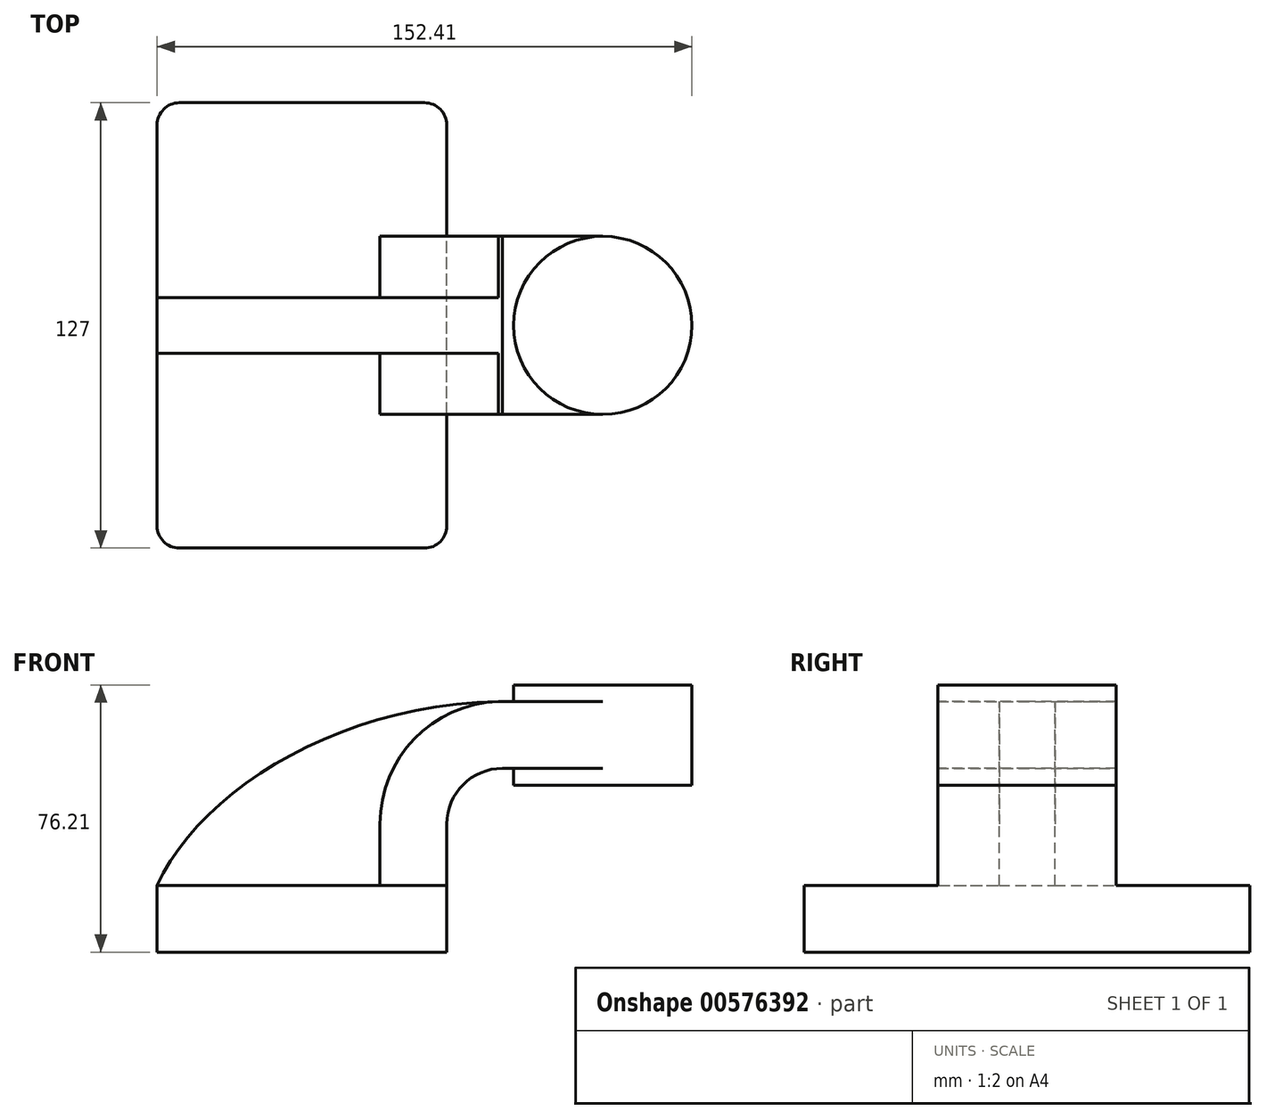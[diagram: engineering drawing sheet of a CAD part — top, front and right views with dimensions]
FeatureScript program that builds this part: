
annotation { "Feature Type Name" : "Feature", "Feature Type Description" : "" }
export const myFeature = defineFeature(function(context is Context, id is Id, definition is map)
    precondition{}
    {
        {
            var Q0;
            Q0=qCreatedBy(makeId("Front.planeOp"),FACE);
            var sketch = newSketch(context, id + "F0", { "sketchPlane" : qUnion([Q0])});
            skLineSegment(sketch, "E0.bottom", {"start": v(41.28, 9.52) * mm, "end": v(-41.28, 9.53) * mm});
            skLineSegment(sketch, "E0.top", {"start": v(41.28, -9.53) * mm, "end": v(-41.27, -9.52) * mm});
            skLineSegment(sketch, "E0.left", {"start": v(41.28, 9.52) * mm, "end": v(41.28, -9.53) * mm});
            skLineSegment(sketch, "E0.right", {"start": v(-41.28, 9.52) * mm, "end": v(-41.28, -9.52) * mm});
            skPoint(sketch, "E0.middle", {"position": v(0, 0) * mm});
            skLineSegment(sketch, "E1.bottom", {"start": v(111.13, 66.67) * mm, "end": v(60.33, 66.67) * mm});
            skLineSegment(sketch, "E1.top", {"start": v(111.13, 38.1) * mm, "end": v(60.33, 38.1) * mm});
            skLineSegment(sketch, "E1.left", {"start": v(111.13, 66.67) * mm, "end": v(111.13, 38.1) * mm});
            skLineSegment(sketch, "E1.right", {"start": v(60.33, 66.67) * mm, "end": v(60.33, 38.1) * mm});
            skPoint(sketch, "E1.middle", {"position": v(85.73, 52.39) * mm});
            skLineSegment(sketch, "E2", {"start": v(41.28, 9.52) * mm, "end": v(41.28, 27) * mm});
            skArc(sketch, "E3", {"start": v(41.28, 27) * mm, "mid": v(45.92, 38.23) * mm, "end": v(57.15, 42.88) * mm});
            skLineSegment(sketch, "E4", {"start": v(57.15, 42.88) * mm, "end": v(85.73, 42.88) * mm});
            skLineSegment(sketch, "E5.0", {"start": v(57.15, 61.93) * mm, "end": v(85.73, 61.93) * mm});
            skArc(sketch, "E5.1", {"start": v(22.23, 27) * mm, "mid": v(32.45, 51.7) * mm, "end": v(57.15, 61.93) * mm});
            skLineSegment(sketch, "E5.2", {"start": v(22.22, 9.52) * mm, "end": v(22.22, 27) * mm});
            skLineSegment(sketch, "E6", {"start": v(85.73, 38.1) * mm, "end": v(85.73, 66.67) * mm});
            skFitSpline(sketch, "E7", {"points": [v(-41.28, 9.52) * mm, v(57.15, 61.93) * mm], "startDerivative": vector(37.56, 80.88) * mm, "endDerivative": vector(141.46, 1.83) * mm});
            skSolve(sketch);
        }
        {
            var Q0;
            Q0=makeQuery(id+"F0.imprint","IMPRINT",FACE,{"disambiguationData":[TD([[makeQuery(id+"F0.imprint","IMPRINT",EDGE,{"derivedFrom":sQuery(id+"F0.wireOp",EDGE,"E0.top")}),-1.0]])]});
            extrude(context, id + "F1", {"entities" : qUnion([Q0]), "endBound" : BoundingType.SYMMETRIC, "depth" : 127 * mm, "offsetDistance" : 25.4 * mm});
        }
        {
            var Q0;
            {var subQ1=sQuery(id+"F0.wireOp",EDGE,"E2");Q0=makeQuery(id+"F0.imprint","IMPRINT",FACE,{"disambiguationData":[TD([[makeQuery(id+"F0.imprint","IMPRINT",EDGE,{"derivedFrom":subQ1}),1.0]])]});}
            var Q1;
            {var subQ0=sQuery(id+"F0.wireOp",EDGE,"E5.0");var subQ1=sQuery(id+"F0.wireOp",EDGE,"E1.right");var subQ2=makeQuery(id+"F0.imprint","INTERSECT",VERTEX,{"derivedFrom":[subQ1,subQ0]});Q1=makeQuery(id+"F0.imprint","IMPRINT",FACE,{"disambiguationData":[TD([[makeQuery(id+"F0.imprint","IMPRINT",EDGE,{"disambiguationData":[TD([[subQ2,-1.0]])],"derivedFrom":subQ1}),1.0]])]});}
            extrude(context, id + "F2", {"entities" : qUnion([Q0, Q1]), "operationType" : NewBodyOperationType.ADD, "endBound" : BoundingType.SYMMETRIC, "depth" : 50.8 * mm, "offsetDistance" : 25.4 * mm});
        }
        {
            var Q0;
            {var subQ3=sQuery(id+"F0.wireOp",EDGE,"E5.2");Q0=makeQuery(id+"F0.imprint","IMPRINT",FACE,{"disambiguationData":[TD([[makeQuery(id+"F0.imprint","IMPRINT",EDGE,{"derivedFrom":subQ3}),1.0]])]});}
            extrude(context, id + "F3", {"entities" : qUnion([Q0]), "operationType" : NewBodyOperationType.ADD, "endBound" : BoundingType.SYMMETRIC, "depth" : 15.88 * mm, "offsetDistance" : 25.4 * mm});
        }
        {
            var Q0;
            {var subQ0=sQuery(id+"F0.wireOp",EDGE,"E1.left");Q0=makeQuery(id+"F0.imprint","IMPRINT",FACE,{"disambiguationData":[TD([[makeQuery(id+"F0.imprint","IMPRINT",EDGE,{"derivedFrom":subQ0}),-1.0]])]});}
            var Q1;
            Q1=sQuery(id+"F0.wireOp",EDGE,"E6");
            revolve(context, id + "F4", {"operationType" : NewBodyOperationType.ADD, "entities" : qUnion([Q0]), "axis" : qUnion([Q1]), "revolveType" : RevolveType.FULL});
        }
        {
            var Q0;
            Q0=makeQuery(id+"F1.opExtrude","CAP_EDGE",EDGE,{"disambiguationData":[OSD([sQuery(id+"F0.wireOp",EDGE,"E0.left")])],"isStart":false});
            var Q1;
            Q1=makeQuery(id+"F1.opExtrude","CAP_EDGE",EDGE,{"disambiguationData":[OSD([sQuery(id+"F0.wireOp",EDGE,"E0.right")])],"isStart":false});
            var Q2;
            Q2=makeQuery(id+"F1.opExtrude","CAP_EDGE",EDGE,{"disambiguationData":[OSD([sQuery(id+"F0.wireOp",EDGE,"E0.right")])],"isStart":true});
            var Q3;
            Q3=makeQuery(id+"F1.opExtrude","CAP_EDGE",EDGE,{"disambiguationData":[OSD([sQuery(id+"F0.wireOp",EDGE,"E0.left")])],"isStart":true});
            fillet(context, id + "F5", {"entities" : qUnion([Q0, Q1, Q2, Q3]), "radius" : 6.35 * mm, "tangentPropagation" : true, "allowEdgeOverflow" : false});
        }
    });
